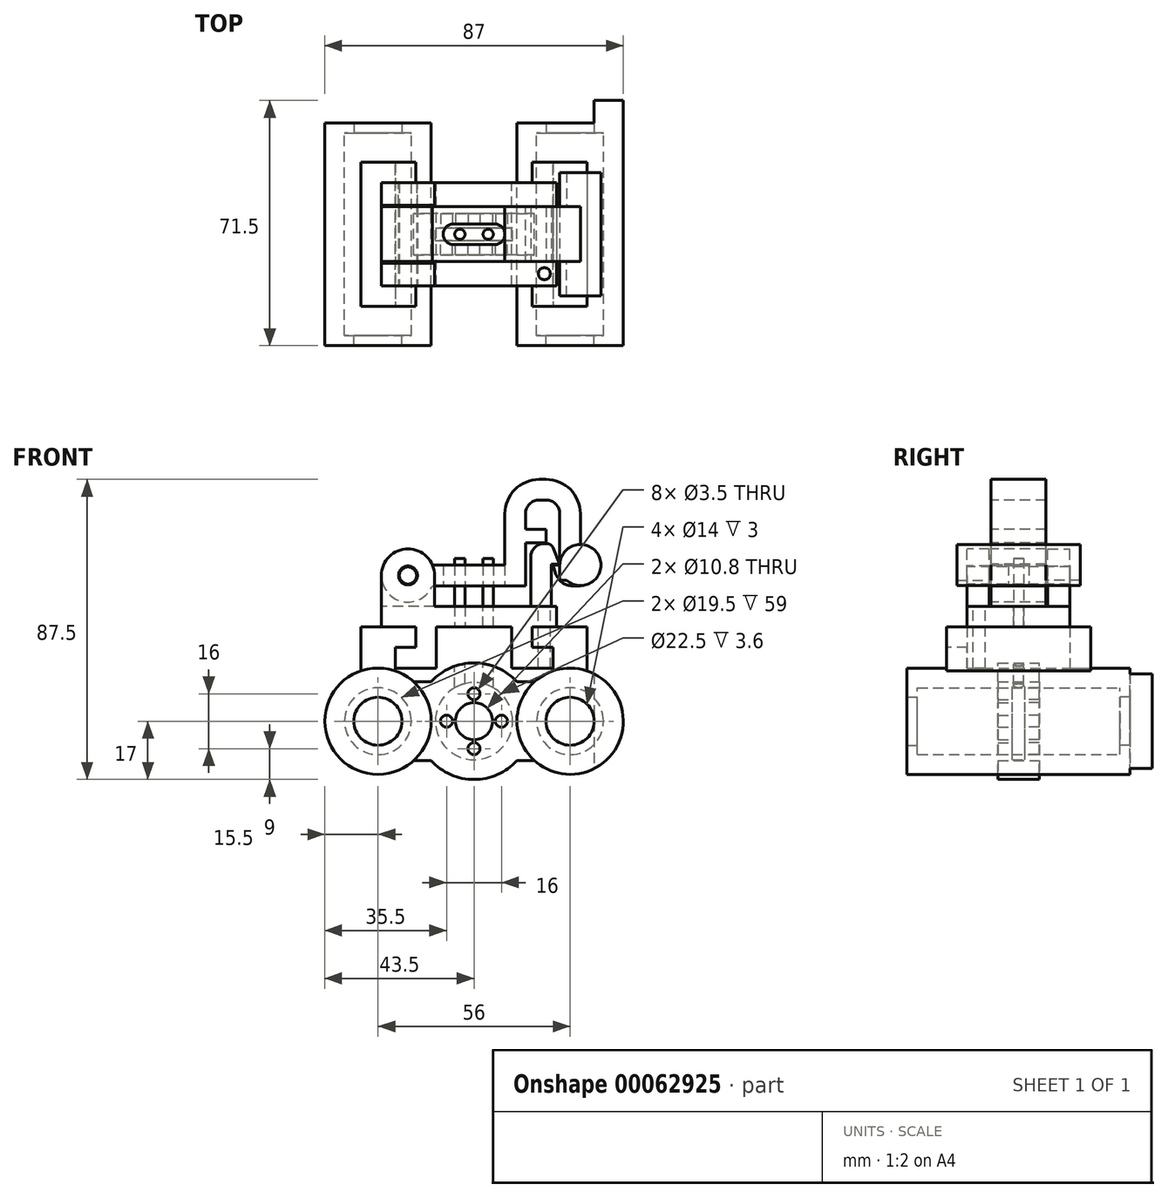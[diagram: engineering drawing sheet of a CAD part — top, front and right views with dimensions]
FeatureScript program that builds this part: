
annotation { "Feature Type Name" : "Feature", "Feature Type Description" : "" }
export const myFeature = defineFeature(function(context is Context, id is Id, definition is map)
    precondition{}
    {
        {
            var Q0;
            Q0=qCreatedBy(makeId("Front.planeOp"),FACE);
            var sketch = newSketch(context, id + "F0", { "sketchPlane" : qUnion([Q0])});
            skCircle(sketch, "E0", {"center": v(0, 0) * mm, "radius": 5.4 * mm});
            skCircle(sketch, "E1", {"center": v(0, 0) * mm, "radius": 11.25 * mm});
            skCircle(sketch, "E2", {"center": v(0, 0) * mm, "radius": 8 * mm, "construction": true});
            skCircle(sketch, "E3", {"center": v(0, 8) * mm, "radius": 1.75 * mm});
            skCircle(sketch, "E4", {"center": v(8, 0) * mm, "radius": 1.75 * mm});
            skCircle(sketch, "E5", {"center": v(0, -8) * mm, "radius": 1.75 * mm});
            skCircle(sketch, "E6", {"center": v(-8, 0) * mm, "radius": 1.75 * mm});
            skArc(sketch, "E7", {"start": v(12.52, 11.5) * mm, "mid": v(0, 17) * mm, "end": v(-12.52, 11.5) * mm});
            skLineSegment(sketch, "E8.bottom", {"start": v(-12.52, 11.5) * mm, "end": v(-17.6, 11.5) * mm});
            skLineSegment(sketch, "E8.top", {"start": v(-12.52, -11.5) * mm, "end": v(-17.6, -11.5) * mm});
            skLineSegment(sketch, "E8.left", {"start": v(-12.52, 11.5) * mm, "end": v(-12.52, -11.5) * mm, "construction": true});
            skLineSegment(sketch, "E9.bottom", {"start": v(12.52, 11.5) * mm, "end": v(17.6, 11.5) * mm});
            skLineSegment(sketch, "E9.top", {"start": v(12.52, -11.5) * mm, "end": v(17.6, -11.5) * mm});
            skLineSegment(sketch, "E9.left", {"start": v(12.52, 11.5) * mm, "end": v(12.52, -11.5) * mm, "construction": true});
            skArc(sketch, "E10", {"start": v(-17.6, 11.5) * mm, "mid": v(-43.5, 0) * mm, "end": v(-17.6, -11.5) * mm});
            skArc(sketch, "E11", {"start": v(17.6, -11.5) * mm, "mid": v(43.5, 0) * mm, "end": v(17.6, 11.5) * mm});
            skCircle(sketch, "E12", {"center": v(-28, 0) * mm, "radius": 9.75 * mm});
            skCircle(sketch, "E13", {"center": v(28, 0) * mm, "radius": 9.75 * mm});
            skLineSegment(sketch, "E14", {"start": v(-28, 0) * mm, "end": v(28, 0) * mm, "construction": true});
            skPoint(sketch, "E15", {"position": v(12.52, 0) * mm});
            skPoint(sketch, "E16", {"position": v(-12.52, 0) * mm});
            skArc(sketch, "E17.trimOffspring", {"start": v(-12.52, -11.5) * mm, "mid": v(0, -17) * mm, "end": v(12.52, -11.5) * mm});
            skSolve(sketch);
        }
        {
            var Q0;
            Q0=makeQuery(id+"F0.imprint","IMPRINT",FACE,{"disambiguationData":[TD([[makeQuery(id+"F0.imprint","IMPRINT",EDGE,{"derivedFrom":sQuery(id+"F0.wireOp",EDGE,"E1")}),-1.0]])]});
            var Q1;
            Q1=makeQuery(id+"F0.imprint","IMPRINT",FACE,{"disambiguationData":[TD([[makeQuery(id+"F0.imprint","IMPRINT",EDGE,{"derivedFrom":sQuery(id+"F0.wireOp",EDGE,"E0")}),-1.0]])]});
            extrude(context, id + "F1", {"entities" : qUnion([Q0, Q1]), "depth" : 6 * mm});
        }
        {
            var Q0;
            Q0=makeQuery(id+"F0.imprint","IMPRINT",FACE,{"disambiguationData":[TD([[makeQuery(id+"F0.imprint","IMPRINT",EDGE,{"derivedFrom":sQuery(id+"F0.wireOp",EDGE,"E0")}),-1.0]])]});
            extrude(context, id + "F2", {"entities" : qUnion([Q0]), "operationType" : NewBodyOperationType.REMOVE, "depth" : 1.8 * mm});
        }
        {
            var Q0;
            Q0=makeQuery(id+"F1.opExtrude","CAP_FACE",FACE,{"disambiguationData":[OSD([sQuery(id+"F0.wireOp",EDGE,"E0"),sQuery(id+"F0.wireOp",EDGE,"E3"),sQuery(id+"F0.wireOp",EDGE,"E4"),sQuery(id+"F0.wireOp",EDGE,"E5"),sQuery(id+"F0.wireOp",EDGE,"E6"),sQuery(id+"F0.wireOp",EDGE,"E7"),sQuery(id+"F0.wireOp",EDGE,"E8.bottom"),sQuery(id+"F0.wireOp",EDGE,"E8.top"),sQuery(id+"F0.wireOp",EDGE,"E9.bottom"),sQuery(id+"F0.wireOp",EDGE,"E9.top"),sQuery(id+"F0.wireOp",EDGE,"E10"),sQuery(id+"F0.wireOp",EDGE,"E11"),sQuery(id+"F0.wireOp",EDGE,"E12"),sQuery(id+"F0.wireOp",EDGE,"E13"),sQuery(id+"F0.wireOp",EDGE,"E17.trimOffspring")])],"isStart":false});
            var sketch = newSketch(context, id + "F3", { "sketchPlane" : qUnion([Q0])});
            skCircle(sketch, "E18", {"center": v(-28, 0) * mm, "radius": 15.5 * mm});
            skCircle(sketch, "E19", {"center": v(-28, 0) * mm, "radius": 9.75 * mm});
            skCircle(sketch, "E20", {"center": v(28, 0) * mm, "radius": 9.75 * mm});
            skCircle(sketch, "E21", {"center": v(28, 0) * mm, "radius": 15.5 * mm});
            skSolve(sketch);
        }
        {
            var Q0;
            Q0 = qSketchRegion(id + "F3", true);
            extrude(context, id + "F4", {"entities" : qUnion([Q0]), "operationType" : NewBodyOperationType.ADD, "depth" : 23.5 * mm});
        }
        {
            var Q0;
            Q0=makeQuery(id+"F4.opExtrude","CAP_FACE",FACE,{"disambiguationData":[OSD([sQuery(id+"F3.wireOp",EDGE,"E18"),sQuery(id+"F3.wireOp",EDGE,"E19")])],"isStart":false});
            var sketch = newSketch(context, id + "F5", { "sketchPlane" : qUnion([Q0])});
            skCircle(sketch, "E22", {"center": v(-28, 0) * mm, "radius": 15.5 * mm});
            skCircle(sketch, "E23", {"center": v(-28, 0) * mm, "radius": 7 * mm});
            skSolve(sketch);
        }
        {
            var Q0;
            Q0 = qSketchRegion(id + "F5", true);
            extrude(context, id + "F6", {"entities" : qUnion([Q0]), "operationType" : NewBodyOperationType.ADD, "depth" : 3 * mm});
        }
        {
            var Q0;
            Q0=makeQuery(id+"F4.opExtrude","CAP_FACE",FACE,{"disambiguationData":[OSD([sQuery(id+"F3.wireOp",EDGE,"E20"),sQuery(id+"F3.wireOp",EDGE,"E21")])],"isStart":false});
            var sketch = newSketch(context, id + "F7", { "sketchPlane" : qUnion([Q0])});
            skCircle(sketch, "E24", {"center": v(28, 0) * mm, "radius": 15.5 * mm});
            skCircle(sketch, "E25", {"center": v(28, 0) * mm, "radius": 7 * mm});
            skSolve(sketch);
        }
        {
            var Q0;
            Q0 = qSketchRegion(id + "F7", true);
            extrude(context, id + "F8", {"entities" : qUnion([Q0]), "operationType" : NewBodyOperationType.ADD, "depth" : 3 * mm});
        }
        {
            var Q0;
            {var subQ0=sQuery(id+"F5.wireOp",EDGE,"E22");Q0=makeQuery(id+"F11.boolean.opBoolean","MERGE",FACE,{"derivedFrom":[makeQuery(id+"F6.opExtrude","CAP_FACE",FACE,{"disambiguationData":[OSD([subQ0,sQuery(id+"F5.wireOp",EDGE,"E23")])],"isStart":false}),makeQuery(id+"F11.opExtrude","CAP_FACE",FACE,{"disambiguationData":[OSD([subQ0,sQuery(id+"F10.wireOp",EDGE,"E26.top"),sQuery(id+"F10.wireOp",EDGE,"E26.left"),sQuery(id+"F10.wireOp",EDGE,"E26.right"),sQuery(id+"F10.wireOp",EDGE,"E27.bottom"),sQuery(id+"F10.wireOp",EDGE,"E27.top"),sQuery(id+"F10.wireOp",EDGE,"E27.right")])],"isStart":true})]});}
            cPlane(context, id + "F9", {"entities" : qUnion([Q0]), "cplaneType" : CPlaneType.OFFSET, "offset" : 11.5 * mm, "oppositeDirection" : true, "width" : 150 * mm, "height" : 150 * mm});
        }
        {
            var Q0;
            Q0=qCreatedBy(id+"F9.planeOp",FACE);
            var sketch = newSketch(context, id + "F10", { "sketchPlane" : qUnion([Q0])});
            skLineSegment(sketch, "E26.top", {"start": v(-33, 27.5) * mm, "end": v(-23, 27.5) * mm});
            skLineSegment(sketch, "E26.left", {"start": v(-33, 14.67) * mm, "end": v(-33, 27.5) * mm});
            skLineSegment(sketch, "E26.right", {"start": v(-23, 14.67) * mm, "end": v(-23, 21.5) * mm});
            skLineSegment(sketch, "E27.bottom", {"start": v(-23, 27.5) * mm, "end": v(-17, 27.5) * mm});
            skLineSegment(sketch, "E27.top", {"start": v(-23, 21.5) * mm, "end": v(-17, 21.5) * mm});
            skLineSegment(sketch, "E27.right", {"start": v(-17, 27.5) * mm, "end": v(-17, 21.5) * mm});
            skLineSegment(sketch, "E28", {"start": v(-28, 0) * mm, "end": v(-28, 27.5) * mm, "construction": true});
            skLineSegment(sketch, "E29", {"start": v(0, 0) * mm, "end": v(0, 38.75) * mm, "construction": true});
            skLineSegment(sketch, "E30.MirrorCS", {"start": v(17, 27.5) * mm, "end": v(17, 21.5) * mm});
            skLineSegment(sketch, "E31.MirrorCS", {"start": v(23, 21.5) * mm, "end": v(17, 21.5) * mm});
            skLineSegment(sketch, "E32.MirrorCS", {"start": v(23, 27.5) * mm, "end": v(17, 27.5) * mm});
            skLineSegment(sketch, "E33.MirrorCS", {"start": v(23, 14.67) * mm, "end": v(23, 21.5) * mm});
            skLineSegment(sketch, "E34.MirrorCS", {"start": v(33, 14.67) * mm, "end": v(33, 27.5) * mm});
            skLineSegment(sketch, "E35.MirrorCS", {"start": v(33, 27.5) * mm, "end": v(23, 27.5) * mm});
            skArc(sketch, "E36", {"start": v(33, 14.67) * mm, "mid": v(28, 15.5) * mm, "end": v(23, 14.67) * mm});
            skArc(sketch, "E37", {"start": v(-23, 14.67) * mm, "mid": v(-28, 15.5) * mm, "end": v(-33, 14.67) * mm});
            skSolve(sketch);
        }
        {
            var Q0;
            Q0 = qSketchRegion(id + "F10", true);
            var Q1;
            Q1=makeQuery(id+"F10.imprint","IMPRINT",FACE,{"disambiguationData":[TD([[makeQuery(id+"F10.imprint","IMPRINT",EDGE,{"derivedFrom":sQuery(id+"F10.wireOp",EDGE,"E26.top")}),-1.0]])]});
            var Q2;
            Q2=makeQuery(id+"F1.opExtrude","CAP_FACE",FACE,{"disambiguationData":[OSD([sQuery(id+"F0.wireOp",EDGE,"E0"),sQuery(id+"F0.wireOp",EDGE,"E3"),sQuery(id+"F0.wireOp",EDGE,"E4"),sQuery(id+"F0.wireOp",EDGE,"E5"),sQuery(id+"F0.wireOp",EDGE,"E6"),sQuery(id+"F0.wireOp",EDGE,"E7"),sQuery(id+"F0.wireOp",EDGE,"E8.bottom"),sQuery(id+"F0.wireOp",EDGE,"E8.top"),sQuery(id+"F0.wireOp",EDGE,"E9.bottom"),sQuery(id+"F0.wireOp",EDGE,"E9.top"),sQuery(id+"F0.wireOp",EDGE,"E10"),sQuery(id+"F0.wireOp",EDGE,"E11"),sQuery(id+"F0.wireOp",EDGE,"E12"),sQuery(id+"F0.wireOp",EDGE,"E13"),sQuery(id+"F0.wireOp",EDGE,"E17.trimOffspring")])],"isStart":true});
            extrude(context, id + "F11", {"entities" : qUnion([Q0, Q1]), "operationType" : NewBodyOperationType.ADD, "endBound" : BoundingType.UP_TO_SURFACE, "oppositeDirection" : true, "endBoundEntityFace" : qUnion([Q2]), "depth" : 25 * mm});
        }
        {
            var Q0;
            Q0=makeQuery(id+"F1.opExtrude","SWEPT_BODY",BODY,{"disambiguationData":[OSD([sQuery(id+"F0.wireOp",EDGE,"E0"),sQuery(id+"F0.wireOp",EDGE,"E3"),sQuery(id+"F0.wireOp",EDGE,"E4"),sQuery(id+"F0.wireOp",EDGE,"E5"),sQuery(id+"F0.wireOp",EDGE,"E6"),sQuery(id+"F0.wireOp",EDGE,"E7"),sQuery(id+"F0.wireOp",EDGE,"E8.bottom"),sQuery(id+"F0.wireOp",EDGE,"E8.top"),sQuery(id+"F0.wireOp",EDGE,"E9.bottom"),sQuery(id+"F0.wireOp",EDGE,"E9.top"),sQuery(id+"F0.wireOp",EDGE,"E10"),sQuery(id+"F0.wireOp",EDGE,"E11"),sQuery(id+"F0.wireOp",EDGE,"E12"),sQuery(id+"F0.wireOp",EDGE,"E13"),sQuery(id+"F0.wireOp",EDGE,"E17.trimOffspring")])]});
            var Q1;
            Q1=qCreatedBy(makeId("Front.planeOp"),FACE);
            mirror(context, id + "F12", {"entities" : qUnion([Q0]), "mirrorPlane" : qUnion([Q1])});
        }
        {
            var Q0;
            Q0=makeQuery(id+"F12.opPattern","COPY",FACE,{"derivedFrom":makeQuery(id+"F11.opExtrude","SWEPT_FACE",FACE,{"disambiguationData":[OSD([sQuery(id+"F10.wireOp",EDGE,"E32.MirrorCS"),sQuery(id+"F10.wireOp",EDGE,"E35.MirrorCS")])]}),"instanceName":"1"});
            var sketch = newSketch(context, id + "F13", { "sketchPlane" : qUnion([Q0])});
            skLineSegment(sketch, "E38.bottom", {"start": v(24, 15) * mm, "end": v(-27, 15) * mm});
            skLineSegment(sketch, "E38.top", {"start": v(24, -15) * mm, "end": v(-27, -15) * mm});
            skLineSegment(sketch, "E38.left", {"start": v(24, 15) * mm, "end": v(24, -15) * mm});
            skLineSegment(sketch, "E38.right", {"start": v(-27, 15) * mm, "end": v(-27, -15) * mm});
            skPoint(sketch, "E39", {"position": v(24, 0) * mm});
            skSolve(sketch);
        }
        {
            var Q0;
            Q0 = qSketchRegion(id + "F13", true);
            extrude(context, id + "F14", {"entities" : qUnion([Q0]), "depth" : 6 * mm});
        }
        {
            var Q0;
            Q0=makeQuery(id+"F14.opExtrude","CAP_FACE",FACE,{"disambiguationData":[OSD([sQuery(id+"F13.wireOp",EDGE,"E38.bottom"),sQuery(id+"F13.wireOp",EDGE,"E38.top"),sQuery(id+"F13.wireOp",EDGE,"E38.left"),sQuery(id+"F13.wireOp",EDGE,"E38.right")])],"isStart":false});
            var sketch = newSketch(context, id + "F15", { "sketchPlane" : qUnion([Q0])});
            skCircle(sketch, "E40", {"center": v(-4.12, 0) * mm, "radius": 1.5 * mm});
            skCircle(sketch, "E41", {"center": v(4.12, 0) * mm, "radius": 1.5 * mm});
            skLineSegment(sketch, "E42", {"start": v(-4.12, 0) * mm, "end": v(4.12, 0) * mm, "construction": true});
            skSolve(sketch);
        }
        {
            var Q0;
            Q0 = qSketchRegion(id + "F15", true);
            extrude(context, id + "F16", {"entities" : qUnion([Q0]), "operationType" : NewBodyOperationType.REMOVE, "oppositeDirection" : true, "depth" : 25 * mm});
        }
        {
            var Q0;
            Q0=makeQuery(id+"F14.opExtrude","CAP_FACE",FACE,{"disambiguationData":[OSD([sQuery(id+"F13.wireOp",EDGE,"E38.bottom"),sQuery(id+"F13.wireOp",EDGE,"E38.top"),sQuery(id+"F13.wireOp",EDGE,"E38.left"),sQuery(id+"F13.wireOp",EDGE,"E38.right")])],"isStart":true});
            var sketch = newSketch(context, id + "F17", { "sketchPlane" : qUnion([Q0])});
            skCircle(sketch, "E43", {"center": v(-4.12, 0) * mm, "radius": 1.5 * mm});
            skCircle(sketch, "E44", {"center": v(4.12, 0) * mm, "radius": 1.5 * mm});
            skSolve(sketch);
        }
        {
            var Q0;
            Q0 = qSketchRegion(id + "F17", true);
            extrude(context, id + "F18", {"entities" : qUnion([Q0]), "oppositeDirection" : true, "depth" : 20 * mm});
        }
        {
            var Q0;
            Q0=makeQuery(id+"F14.opExtrude","CAP_FACE",FACE,{"disambiguationData":[OSD([sQuery(id+"F13.wireOp",EDGE,"E38.bottom"),sQuery(id+"F13.wireOp",EDGE,"E38.top"),sQuery(id+"F13.wireOp",EDGE,"E38.left"),sQuery(id+"F13.wireOp",EDGE,"E38.right")])],"isStart":false});
            cPlane(context, id + "F19", {"entities" : qUnion([Q0]), "cplaneType" : CPlaneType.OFFSET, "offset" : 6 * mm, "width" : 150 * mm, "height" : 150 * mm});
        }
        {
            var Q0;
            Q0=qCreatedBy(id+"F19.planeOp",FACE);
            var sketch = newSketch(context, id + "F20", { "sketchPlane" : qUnion([Q0])});
            skLineSegment(sketch, "E45.bottom", {"start": v(-19.25, -8) * mm, "end": v(15, -8) * mm});
            skLineSegment(sketch, "E45.top", {"start": v(-19.25, 8) * mm, "end": v(15, 8) * mm});
            skLineSegment(sketch, "E45.left", {"start": v(-19.25, -8) * mm, "end": v(-19.25, 8) * mm});
            skLineSegment(sketch, "E45.right", {"start": v(15, -8) * mm, "end": v(15, 8) * mm});
            skLineSegment(sketch, "E46.bottom", {"start": v(-6, -3) * mm, "end": v(6, -3) * mm});
            skLineSegment(sketch, "E46.top", {"start": v(-6, 3) * mm, "end": v(6, 3) * mm});
            skArc(sketch, "E47", {"start": v(-6, -3) * mm, "mid": v(-9, 0) * mm, "end": v(-6, 3) * mm});
            skArc(sketch, "E48", {"start": v(6, -3) * mm, "mid": v(9, 0) * mm, "end": v(6, 3) * mm});
            skLineSegment(sketch, "E49", {"start": v(-19.25, 0) * mm, "end": v(15, 0) * mm, "construction": true});
            skSolve(sketch);
        }
        {
            var Q0;
            Q0 = qSketchRegion(id + "F20", true);
            extrude(context, id + "F21", {"entities" : qUnion([Q0]), "depth" : 6 * mm});
        }
        {
            var Q0;
            Q0=makeQuery(id+"F21.opExtrude","SWEPT_FACE",FACE,{"disambiguationData":[OSD([sQuery(id+"F20.wireOp",EDGE,"E45.bottom")])]});
            var sketch = newSketch(context, id + "F22", { "sketchPlane" : qUnion([Q0])});
            skCircle(sketch, "E50", {"center": v(-19.25, 42.5) * mm, "radius": 2.75 * mm});
            skCircle(sketch, "E51", {"center": v(-19.25, 42.5) * mm, "radius": 7.75 * mm});
            skSolve(sketch);
        }
        {
            var Q0;
            {var subQ0=sQuery(id+"F20.wireOp",EDGE,"E45.bottom");var subQ6=sQuery(id+"F22.wireOp",EDGE,"E51");var subQ7=makeQuery(id+"F21.opExtrude","CAP_EDGE",EDGE,{"disambiguationData":[OSD([subQ0])],"isStart":true});var subQ8=makeQuery(id+"F22.imprint","INTERSECT",VERTEX,{"derivedFrom":[subQ7,subQ6]});Q0=makeQuery(id+"F22.imprint","IMPRINT",FACE,{"disambiguationData":[TD([[makeQuery(id+"F22.imprint","IMPRINT",EDGE,{"disambiguationData":[TD([[subQ8,1.0]])],"derivedFrom":subQ6}),1.0]])]});}
            var Q1;
            Q1=makeQuery(id+"F21.opExtrude","SWEPT_FACE",FACE,{"disambiguationData":[OSD([sQuery(id+"F20.wireOp",EDGE,"E45.top")])]});
            extrude(context, id + "F23", {"entities" : qUnion([Q0]), "operationType" : NewBodyOperationType.ADD, "endBound" : BoundingType.UP_TO_SURFACE, "oppositeDirection" : true, "endBoundEntityFace" : qUnion([Q1]), "depth" : 25 * mm});
        }
        {
            var Q0;
            {var subQ0=sQuery(id+"F22.wireOp",EDGE,"E50");var subQ1=makeQuery(id+"F21.opExtrude","SWEPT_EDGE",EDGE,{"disambiguationData":[OSD([sQuery(id+"F20.wireOp",EDGE,"E45.bottom"),sQuery(id+"F20.wireOp",EDGE,"E45.left")])]});var subQ2=makeQuery(id+"F22.imprint","INTERSECT",VERTEX,{"disambiguationData":[OD(0.0)],"derivedFrom":[subQ1,subQ0]});Q0=makeQuery(id+"F22.imprint","IMPRINT",FACE,{"disambiguationData":[TD([[makeQuery(id+"F22.imprint","IMPRINT",EDGE,{"disambiguationData":[TD([[subQ2,-1.0]])],"derivedFrom":subQ0}),1.0]])]});}
            var Q1;
            Q1=makeQuery(id+"F23.boolean.opBoolean","MERGE",FACE,{"derivedFrom":[makeQuery(id+"F21.opExtrude","SWEPT_FACE",FACE,{"disambiguationData":[OSD([sQuery(id+"F20.wireOp",EDGE,"E45.top")])]}),makeQuery(id+"F23.opExtrude","CAP_FACE",FACE,{"disambiguationData":[OSD([sQuery(id+"F20.wireOp",EDGE,"E45.bottom"),sQuery(id+"F20.wireOp",EDGE,"E45.left"),sQuery(id+"F22.wireOp",EDGE,"E50"),sQuery(id+"F22.wireOp",EDGE,"E51")])],"isStart":false})]});
            extrude(context, id + "F24", {"entities" : qUnion([Q0]), "operationType" : NewBodyOperationType.REMOVE, "endBound" : BoundingType.UP_TO_SURFACE, "oppositeDirection" : true, "endBoundEntityFace" : qUnion([Q1]), "depth" : 25 * mm});
        }
        {
            var Q0;
            Q0=makeQuery(id+"F14.opExtrude","SWEPT_FACE",FACE,{"disambiguationData":[OSD([sQuery(id+"F13.wireOp",EDGE,"E38.top")])]});
            var sketch = newSketch(context, id + "F25", { "sketchPlane" : qUnion([Q0])});
            skLineSegment(sketch, "E52.bottom", {"start": v(-27, 33.5) * mm, "end": v(-11.5, 33.5) * mm});
            skLineSegment(sketch, "E52.left", {"start": v(-27, 33.5) * mm, "end": v(-27, 42.5) * mm});
            skLineSegment(sketch, "E52.right", {"start": v(-11.5, 33.5) * mm, "end": v(-11.5, 42.5) * mm});
            skArc(sketch, "E53", {"start": v(-11.5, 42.5) * mm, "mid": v(-19.25, 50.25) * mm, "end": v(-27, 42.5) * mm});
            skCircle(sketch, "E54", {"center": v(-19.25, 42.5) * mm, "radius": 2.75 * mm});
            skSolve(sketch);
        }
        {
            var Q0;
            Q0 = qSketchRegion(id + "F25", true);
            var Q1;
            {var subQ2=sQuery(id+"F25.wireOp",EDGE,"E52.bottom");Q1=makeQuery(id+"F25.imprint","IMPRINT",FACE,{"disambiguationData":[TD([[makeQuery(id+"F25.imprint","IMPRINT",EDGE,{"derivedFrom":subQ2}),1.0]])]});}
            extrude(context, id + "F26", {"entities" : qUnion([Q0, Q1]), "operationType" : NewBodyOperationType.ADD, "oppositeDirection" : true, "depth" : 6.5 * mm});
        }
        {
            var Q0;
            Q0=makeQuery(id+"F14.opExtrude","SWEPT_FACE",FACE,{"disambiguationData":[OSD([sQuery(id+"F13.wireOp",EDGE,"E38.bottom")])]});
            var sketch = newSketch(context, id + "F27", { "sketchPlane" : qUnion([Q0])});
            skLineSegment(sketch, "E55.bottom", {"start": v(27, 33.5) * mm, "end": v(11.5, 33.5) * mm});
            skLineSegment(sketch, "E55.left", {"start": v(27, 33.5) * mm, "end": v(27, 42.5) * mm});
            skLineSegment(sketch, "E55.right", {"start": v(11.5, 33.5) * mm, "end": v(11.5, 42.5) * mm});
            skArc(sketch, "E56", {"start": v(27, 42.5) * mm, "mid": v(19.25, 50.25) * mm, "end": v(11.5, 42.5) * mm});
            skCircle(sketch, "E57", {"center": v(19.25, 42.5) * mm, "radius": 2.75 * mm});
            skSolve(sketch);
        }
        {
            var Q0;
            Q0 = qSketchRegion(id + "F27", true);
            var Q1;
            {var subQ1=sQuery(id+"F27.wireOp",EDGE,"E55.bottom");Q1=makeQuery(id+"F27.imprint","IMPRINT",FACE,{"disambiguationData":[TD([[makeQuery(id+"F27.imprint","IMPRINT",EDGE,{"derivedFrom":subQ1}),-1.0]])]});}
            extrude(context, id + "F28", {"entities" : qUnion([Q0, Q1]), "operationType" : NewBodyOperationType.ADD, "oppositeDirection" : true, "depth" : 6.5 * mm});
        }
        {
            var Q0;
            {var subQ0=sQuery(id+"F13.wireOp",EDGE,"E38.top");Q0=makeQuery(id+"F26.boolean.opBoolean","MERGE",FACE,{"derivedFrom":[makeQuery(id+"F14.opExtrude","SWEPT_FACE",FACE,{"disambiguationData":[OSD([subQ0])]}),makeQuery(id+"F26.opExtrude","CAP_FACE",FACE,{"disambiguationData":[OSD([subQ0,sQuery(id+"F13.wireOp",EDGE,"E38.left"),sQuery(id+"F13.wireOp",EDGE,"E38.right"),sQuery(id+"F25.wireOp",EDGE,"E52.left"),sQuery(id+"F25.wireOp",EDGE,"E52.right"),sQuery(id+"F25.wireOp",EDGE,"E53"),sQuery(id+"F25.wireOp",EDGE,"E54")])],"isStart":true})]});}
            var sketch = newSketch(context, id + "F29", { "sketchPlane" : qUnion([Q0])});
            skCircle(sketch, "E58", {"center": v(-19.25, 42.5) * mm, "radius": 2.5 * mm});
            skSolve(sketch);
        }
        {
            var Q0;
            Q0 = qSketchRegion(id + "F29", true);
            var Q1;
            {var subQ0=sQuery(id+"F13.wireOp",EDGE,"E38.bottom");Q1=makeQuery(id+"F28.boolean.opBoolean","MERGE",FACE,{"derivedFrom":[makeQuery(id+"F14.opExtrude","SWEPT_FACE",FACE,{"disambiguationData":[OSD([subQ0])]}),makeQuery(id+"F28.opExtrude","CAP_FACE",FACE,{"disambiguationData":[OSD([sQuery(id+"F10.wireOp",EDGE,"E34.MirrorCS"),sQuery(id+"F10.wireOp",EDGE,"E35.MirrorCS"),subQ0,sQuery(id+"F13.wireOp",EDGE,"E38.left"),sQuery(id+"F13.wireOp",EDGE,"E38.right"),sQuery(id+"F27.wireOp",EDGE,"E55.left"),sQuery(id+"F27.wireOp",EDGE,"E55.right"),sQuery(id+"F27.wireOp",EDGE,"E56"),sQuery(id+"F27.wireOp",EDGE,"E57")])],"isStart":true})]});}
            extrude(context, id + "F30", {"entities" : qUnion([Q0]), "endBound" : BoundingType.UP_TO_SURFACE, "oppositeDirection" : true, "endBoundEntityFace" : qUnion([Q1]), "depth" : 25 * mm});
        }
        {
            var Q0;
            {var subQ0=sQuery(id+"F20.wireOp",EDGE,"E45.bottom");Q0=makeQuery(id+"F23.boolean.opBoolean","MERGE",FACE,{"derivedFrom":[makeQuery(id+"F21.opExtrude","SWEPT_FACE",FACE,{"disambiguationData":[OSD([subQ0])]}),makeQuery(id+"F23.opExtrude","CAP_FACE",FACE,{"disambiguationData":[OSD([subQ0,sQuery(id+"F20.wireOp",EDGE,"E45.left"),sQuery(id+"F22.wireOp",EDGE,"E50"),sQuery(id+"F22.wireOp",EDGE,"E51")])],"isStart":true})]});}
            var sketch = newSketch(context, id + "F31", { "sketchPlane" : qUnion([Q0])});
            skLineSegment(sketch, "E59", {"start": v(9, 45.5) * mm, "end": v(9, 60.5) * mm});
            skLineSegment(sketch, "E60", {"start": v(19, 70.5) * mm, "end": v(21, 70.5) * mm});
            skLineSegment(sketch, "E61", {"start": v(31, 60.5) * mm, "end": v(31, 39.5) * mm});
            skLineSegment(sketch, "E62", {"start": v(31, 39.5) * mm, "end": v(28.6, 39.5) * mm});
            skLineSegment(sketch, "E63", {"start": v(23.86, 42.92) * mm, "end": v(23, 45.5) * mm});
            skLineSegment(sketch, "E64", {"start": v(23, 45.5) * mm, "end": v(25, 45.5) * mm});
            skLineSegment(sketch, "E65", {"start": v(25, 45.5) * mm, "end": v(25, 60.5) * mm});
            skLineSegment(sketch, "E66", {"start": v(21, 64.5) * mm, "end": v(19, 64.5) * mm});
            skLineSegment(sketch, "E67", {"start": v(15, 60.5) * mm, "end": v(15, 45.5) * mm});
            skPoint(sketch, "E68.visualSharp", {"position": v(9, 70.5) * mm});
            skArc(sketch, "E68.filletArc", {"start": v(19, 70.5) * mm, "mid": v(11.93, 67.57) * mm, "end": v(9, 60.5) * mm});
            skPoint(sketch, "E69.visualSharp", {"position": v(15, 64.5) * mm});
            skArc(sketch, "E69.filletArc", {"start": v(19, 64.5) * mm, "mid": v(16.17, 63.33) * mm, "end": v(15, 60.5) * mm});
            skPoint(sketch, "E70.visualSharp", {"position": v(31, 70.5) * mm});
            skArc(sketch, "E70.filletArc", {"start": v(31, 60.5) * mm, "mid": v(28.07, 67.57) * mm, "end": v(21, 70.5) * mm});
            skPoint(sketch, "E71.visualSharp", {"position": v(25, 64.5) * mm});
            skArc(sketch, "E71.filletArc", {"start": v(25, 60.5) * mm, "mid": v(23.83, 63.33) * mm, "end": v(21, 64.5) * mm});
            skLineSegment(sketch, "E72", {"start": v(9, 45.5) * mm, "end": v(15, 45.5) * mm});
            skLineSegment(sketch, "E73.bottom", {"start": v(15, 56) * mm, "end": v(21, 56) * mm});
            skLineSegment(sketch, "E73.top", {"start": v(15, 52) * mm, "end": v(21, 52) * mm});
            skLineSegment(sketch, "E73.left", {"start": v(15, 56) * mm, "end": v(15, 52) * mm});
            skLineSegment(sketch, "E73.right", {"start": v(21, 56) * mm, "end": v(21, 52) * mm});
            skPoint(sketch, "E74.visualSharp", {"position": v(25, 39.5) * mm});
            skArc(sketch, "E74.filletArc", {"start": v(23.86, 42.92) * mm, "mid": v(25.68, 40.44) * mm, "end": v(28.6, 39.5) * mm});
            skSolve(sketch);
        }
        {
            var Q0;
            Q0 = qSketchRegion(id + "F31", true);
            var Q1;
            Q1=makeQuery(id+"F23.boolean.opBoolean","MERGE",FACE,{"derivedFrom":[makeQuery(id+"F21.opExtrude","SWEPT_FACE",FACE,{"disambiguationData":[OSD([sQuery(id+"F20.wireOp",EDGE,"E45.top")])]}),makeQuery(id+"F23.opExtrude","CAP_FACE",FACE,{"disambiguationData":[OSD([sQuery(id+"F20.wireOp",EDGE,"E45.bottom"),sQuery(id+"F20.wireOp",EDGE,"E45.left"),sQuery(id+"F22.wireOp",EDGE,"E50"),sQuery(id+"F22.wireOp",EDGE,"E51")])],"isStart":false})]});
            extrude(context, id + "F32", {"entities" : qUnion([Q0]), "operationType" : NewBodyOperationType.ADD, "endBound" : BoundingType.UP_TO_SURFACE, "oppositeDirection" : true, "endBoundEntityFace" : qUnion([Q1]), "depth" : 25 * mm});
        }
        {
            var Q0;
            {var subQ0=sQuery(id+"F20.wireOp",EDGE,"E45.bottom");Q0=makeQuery(id+"F32.boolean.opBoolean","MERGE",FACE,{"derivedFrom":[makeQuery(id+"F23.boolean.opBoolean","MERGE",FACE,{"derivedFrom":[makeQuery(id+"F21.opExtrude","SWEPT_FACE",FACE,{"disambiguationData":[OSD([subQ0])]}),makeQuery(id+"F23.opExtrude","CAP_FACE",FACE,{"disambiguationData":[OSD([subQ0,sQuery(id+"F20.wireOp",EDGE,"E45.left"),sQuery(id+"F22.wireOp",EDGE,"E50"),sQuery(id+"F22.wireOp",EDGE,"E51")])],"isStart":true})]}),makeQuery(id+"F32.opExtrude","CAP_FACE",FACE,{"disambiguationData":[OSD([sQuery(id+"F31.wireOp",EDGE,"5079acd1-eaac-4507-bca1-516ebb47fa8f"),sQuery(id+"F31.wireOp",EDGE,"82dcc8e1-da9b-4338-850f-ae2697795ad2"),sQuery(id+"F31.wireOp",EDGE,"v46wGmbz-xF6Q-51pb-38RE-oWoljmZ9v5JP"),sQuery(id+"F31.wireOp",EDGE,"4d731f38-e2de-4b35-94f0-ffd8c3d27091.bottom"),sQuery(id+"F31.wireOp",EDGE,"4d731f38-e2de-4b35-94f0-ffd8c3d27091.left"),sQuery(id+"F31.wireOp",EDGE,"4d731f38-e2de-4b35-94f0-ffd8c3d27091.right"),sQuery(id+"F31.wireOp",EDGE,"0a39d5b3-3a2a-493f-8220-f63ec6ca32e2.bottom"),sQuery(id+"F31.wireOp",EDGE,"0a39d5b3-3a2a-493f-8220-f63ec6ca32e2.top"),sQuery(id+"F31.wireOp",EDGE,"0a39d5b3-3a2a-493f-8220-f63ec6ca32e2.left"),sQuery(id+"F31.wireOp",EDGE,"45f73411-8ce3-4968-b567-3c25bc21c99c.top"),sQuery(id+"F31.wireOp",EDGE,"45f73411-8ce3-4968-b567-3c25bc21c99c.left"),sQuery(id+"F31.wireOp",EDGE,"45f73411-8ce3-4968-b567-3c25bc21c99c.right"),sQuery(id+"F31.wireOp",EDGE,"ByrJsz3G-Q0Oq-3CNk-jIkp-fLPtCC3wEZpb"),sQuery(id+"F31.wireOp",EDGE,"mAN19z1q-9uuv-X1AW-9HnC-pkhjFqnwcaoK")])],"isStart":true})]});}
            var sketch = newSketch(context, id + "F33", { "sketchPlane" : qUnion([Q0])});
            skLineSegment(sketch, "E75.bottom", {"start": v(20.5, 51.8) * mm, "end": v(21.17, 51.8) * mm});
            skLineSegment(sketch, "E75.top", {"start": v(16.5, 33.5) * mm, "end": v(22.5, 33.5) * mm});
            skLineSegment(sketch, "E75.left", {"start": v(16.5, 47.8) * mm, "end": v(16.5, 33.5) * mm});
            skLineSegment(sketch, "E75.right", {"start": v(22.5, 45.8) * mm, "end": v(22.5, 33.5) * mm});
            skLineSegment(sketch, "E76", {"start": v(23.01, 50.57) * mm, "end": v(25, 45.8) * mm});
            skLineSegment(sketch, "E77", {"start": v(22.5, 45.8) * mm, "end": v(25, 45.8) * mm});
            skPoint(sketch, "E78.visualSharp", {"position": v(16.5, 51.8) * mm});
            skArc(sketch, "E78.filletArc", {"start": v(20.5, 51.8) * mm, "mid": v(17.67, 50.63) * mm, "end": v(16.5, 47.8) * mm});
            skPoint(sketch, "E79.visualSharp", {"position": v(22.5, 51.8) * mm});
            skArc(sketch, "E79.filletArc", {"start": v(23.01, 50.57) * mm, "mid": v(22.28, 51.46) * mm, "end": v(21.17, 51.8) * mm});
            skSolve(sketch);
        }
        {
            var Q0;
            Q0 = qSketchRegion(id + "F33", true);
            var Q1;
            Q1=makeQuery(id+"F32.boolean.opBoolean","MERGE",FACE,{"derivedFrom":[makeQuery(id+"F23.boolean.opBoolean","MERGE",FACE,{"derivedFrom":[makeQuery(id+"F21.opExtrude","SWEPT_FACE",FACE,{"disambiguationData":[OSD([sQuery(id+"F20.wireOp",EDGE,"E45.top")])]}),makeQuery(id+"F23.opExtrude","CAP_FACE",FACE,{"disambiguationData":[OSD([sQuery(id+"F20.wireOp",EDGE,"E45.bottom"),sQuery(id+"F20.wireOp",EDGE,"E45.left"),sQuery(id+"F22.wireOp",EDGE,"E50"),sQuery(id+"F22.wireOp",EDGE,"E51")])],"isStart":false})]}),makeQuery(id+"F32.opExtrude","CAP_FACE",FACE,{"disambiguationData":[OSD([sQuery(id+"F31.wireOp",EDGE,"5079acd1-eaac-4507-bca1-516ebb47fa8f"),sQuery(id+"F31.wireOp",EDGE,"82dcc8e1-da9b-4338-850f-ae2697795ad2"),sQuery(id+"F31.wireOp",EDGE,"v46wGmbz-xF6Q-51pb-38RE-oWoljmZ9v5JP"),sQuery(id+"F31.wireOp",EDGE,"4d731f38-e2de-4b35-94f0-ffd8c3d27091.bottom"),sQuery(id+"F31.wireOp",EDGE,"4d731f38-e2de-4b35-94f0-ffd8c3d27091.left"),sQuery(id+"F31.wireOp",EDGE,"4d731f38-e2de-4b35-94f0-ffd8c3d27091.right"),sQuery(id+"F31.wireOp",EDGE,"0a39d5b3-3a2a-493f-8220-f63ec6ca32e2.bottom"),sQuery(id+"F31.wireOp",EDGE,"0a39d5b3-3a2a-493f-8220-f63ec6ca32e2.top"),sQuery(id+"F31.wireOp",EDGE,"0a39d5b3-3a2a-493f-8220-f63ec6ca32e2.left"),sQuery(id+"F31.wireOp",EDGE,"45f73411-8ce3-4968-b567-3c25bc21c99c.top"),sQuery(id+"F31.wireOp",EDGE,"45f73411-8ce3-4968-b567-3c25bc21c99c.left"),sQuery(id+"F31.wireOp",EDGE,"45f73411-8ce3-4968-b567-3c25bc21c99c.right"),sQuery(id+"F31.wireOp",EDGE,"ByrJsz3G-Q0Oq-3CNk-jIkp-fLPtCC3wEZpb"),sQuery(id+"F31.wireOp",EDGE,"mAN19z1q-9uuv-X1AW-9HnC-pkhjFqnwcaoK")])],"isStart":false})]});
            extrude(context, id + "F34", {"entities" : qUnion([Q0]), "operationType" : NewBodyOperationType.ADD, "endBound" : BoundingType.UP_TO_SURFACE, "oppositeDirection" : true, "endBoundEntityFace" : qUnion([Q1]), "depth" : 25 * mm});
        }
        {
            var Q0;
            {var subQ0=sQuery(id+"F13.wireOp",EDGE,"E38.bottom");Q0=makeQuery(id+"F28.boolean.opBoolean","MERGE",FACE,{"derivedFrom":[makeQuery(id+"F14.opExtrude","SWEPT_FACE",FACE,{"disambiguationData":[OSD([subQ0])]}),makeQuery(id+"F28.opExtrude","CAP_FACE",FACE,{"disambiguationData":[OSD([sQuery(id+"F10.wireOp",EDGE,"E34.MirrorCS"),sQuery(id+"F10.wireOp",EDGE,"E35.MirrorCS"),subQ0,sQuery(id+"F13.wireOp",EDGE,"E38.left"),sQuery(id+"F13.wireOp",EDGE,"E38.right"),sQuery(id+"F27.wireOp",EDGE,"E55.left"),sQuery(id+"F27.wireOp",EDGE,"E55.right"),sQuery(id+"F27.wireOp",EDGE,"E56"),sQuery(id+"F27.wireOp",EDGE,"E57")])],"isStart":true})]});}
            var sketch = newSketch(context, id + "F35", { "sketchPlane" : qUnion([Q0])});
            skLineSegment(sketch, "E80.bottom", {"start": v(-11, 27.5) * mm, "end": v(-17, 27.5) * mm});
            skLineSegment(sketch, "E80.top", {"start": v(-11, 15.5) * mm, "end": v(-17, 15.5) * mm});
            skLineSegment(sketch, "E80.left", {"start": v(-11, 27.5) * mm, "end": v(-11, 15.5) * mm});
            skLineSegment(sketch, "E80.right", {"start": v(-17, 27.5) * mm, "end": v(-17, 21.5) * mm});
            skLineSegment(sketch, "E81.bottom", {"start": v(-17, 15.5) * mm, "end": v(-23, 15.5) * mm});
            skLineSegment(sketch, "E81.top", {"start": v(-17, 21.5) * mm, "end": v(-23, 21.5) * mm});
            skLineSegment(sketch, "E81.right", {"start": v(-23, 15.5) * mm, "end": v(-23, 21.5) * mm});
            skLineSegment(sketch, "E82", {"start": v(0, 27.5) * mm, "end": v(0, 19.84) * mm, "construction": true});
            skLineSegment(sketch, "E83.MirrorCS", {"start": v(11, 27.5) * mm, "end": v(11, 15.5) * mm});
            skLineSegment(sketch, "E84.MirrorCS", {"start": v(17, 27.5) * mm, "end": v(17, 21.5) * mm});
            skLineSegment(sketch, "E85.MirrorCS", {"start": v(11, 27.5) * mm, "end": v(17, 27.5) * mm});
            skLineSegment(sketch, "E86.MirrorCS", {"start": v(11, 15.5) * mm, "end": v(17, 15.5) * mm});
            skLineSegment(sketch, "E87.MirrorCS", {"start": v(17, 15.5) * mm, "end": v(23, 15.5) * mm});
            skLineSegment(sketch, "E88.MirrorCS", {"start": v(23, 15.5) * mm, "end": v(23, 21.5) * mm});
            skLineSegment(sketch, "E89.MirrorCS", {"start": v(17, 21.5) * mm, "end": v(23, 21.5) * mm});
            skSolve(sketch);
        }
        {
            var Q0;
            Q0 = qSketchRegion(id + "F35", true);
            var Q1;
            {var subQ0=sQuery(id+"F13.wireOp",EDGE,"E38.top");Q1=makeQuery(id+"F26.boolean.opBoolean","MERGE",FACE,{"derivedFrom":[makeQuery(id+"F14.opExtrude","SWEPT_FACE",FACE,{"disambiguationData":[OSD([subQ0])]}),makeQuery(id+"F26.opExtrude","CAP_FACE",FACE,{"disambiguationData":[OSD([subQ0,sQuery(id+"F13.wireOp",EDGE,"E38.left"),sQuery(id+"F13.wireOp",EDGE,"E38.right"),sQuery(id+"F25.wireOp",EDGE,"E52.bottom"),sQuery(id+"F25.wireOp",EDGE,"E52.left"),sQuery(id+"F25.wireOp",EDGE,"E52.right"),sQuery(id+"F25.wireOp",EDGE,"E53"),sQuery(id+"F25.wireOp",EDGE,"E54")])],"isStart":true})]});}
            extrude(context, id + "F36", {"entities" : qUnion([Q0]), "operationType" : NewBodyOperationType.ADD, "endBound" : BoundingType.UP_TO_SURFACE, "oppositeDirection" : true, "endBoundEntityFace" : qUnion([Q1]), "depth" : 25 * mm});
        }
        {
            var Q0;
            Q0=makeQuery(id+"F11.opExtrude","SWEPT_FACE",FACE,{"disambiguationData":[OSD([sQuery(id+"F10.wireOp",EDGE,"E27.top")])]});
            var sketch = newSketch(context, id + "F37", { "sketchPlane" : qUnion([Q0])});
            skLineSegment(sketch, "E90.rect.bottom", {"start": v(17, -15) * mm, "end": v(23, -15) * mm});
            skLineSegment(sketch, "E90.rect.top", {"start": v(17, -21) * mm, "end": v(23, -21) * mm});
            skLineSegment(sketch, "E90.rect.left", {"start": v(17, -15) * mm, "end": v(17, -21) * mm});
            skLineSegment(sketch, "E90.rect.right", {"start": v(23, -15) * mm, "end": v(23, -21) * mm});
            skPoint(sketch, "E90.rect.middle", {"position": v(20, -18) * mm});
            skLineSegment(sketch, "E91.rect.bottom", {"start": v(-17, -15) * mm, "end": v(-23, -15) * mm});
            skLineSegment(sketch, "E91.rect.top", {"start": v(-17, -21) * mm, "end": v(-23, -21) * mm});
            skLineSegment(sketch, "E91.rect.left", {"start": v(-17, -15) * mm, "end": v(-17, -21) * mm});
            skLineSegment(sketch, "E91.rect.right", {"start": v(-23, -15) * mm, "end": v(-23, -21) * mm});
            skPoint(sketch, "E91.rect.middle", {"position": v(-20, -18) * mm});
            skSolve(sketch);
        }
        {
            var Q0;
            Q0 = qSketchRegion(id + "F37", true);
            extrude(context, id + "F38", {"entities" : qUnion([Q0]), "operationType" : NewBodyOperationType.ADD, "depth" : 6 * mm});
        }
        {
            var Q0;
            Q0=makeQuery(id+"F32.boolean.opBoolean","MERGE",FACE,{"derivedFrom":[makeQuery(id+"F23.boolean.opBoolean","MERGE",FACE,{"derivedFrom":[makeQuery(id+"F21.opExtrude","SWEPT_FACE",FACE,{"disambiguationData":[OSD([sQuery(id+"F20.wireOp",EDGE,"E45.top")])]}),makeQuery(id+"F23.opExtrude","CAP_FACE",FACE,{"disambiguationData":[OSD([sQuery(id+"F20.wireOp",EDGE,"E45.bottom"),sQuery(id+"F20.wireOp",EDGE,"E45.left"),sQuery(id+"F22.wireOp",EDGE,"E50"),sQuery(id+"F22.wireOp",EDGE,"E51")])],"isStart":false})]}),makeQuery(id+"F32.opExtrude","CAP_FACE",FACE,{"disambiguationData":[OSD([sQuery(id+"F31.wireOp",EDGE,"E59"),sQuery(id+"F31.wireOp",EDGE,"E60"),sQuery(id+"F31.wireOp",EDGE,"E61"),sQuery(id+"F31.wireOp",EDGE,"E62"),sQuery(id+"F31.wireOp",EDGE,"E63"),sQuery(id+"F31.wireOp",EDGE,"E64"),sQuery(id+"F31.wireOp",EDGE,"E65"),sQuery(id+"F31.wireOp",EDGE,"E66"),sQuery(id+"F31.wireOp",EDGE,"E67"),sQuery(id+"F31.wireOp",EDGE,"E68.filletArc"),sQuery(id+"F31.wireOp",EDGE,"E69.filletArc"),sQuery(id+"F31.wireOp",EDGE,"E70.filletArc"),sQuery(id+"F31.wireOp",EDGE,"E71.filletArc"),sQuery(id+"F31.wireOp",EDGE,"E72"),sQuery(id+"F31.wireOp",EDGE,"E73.bottom"),sQuery(id+"F31.wireOp",EDGE,"E73.top"),sQuery(id+"F31.wireOp",EDGE,"E73.right"),sQuery(id+"F31.wireOp",EDGE,"E74.filletArc")])],"isStart":false})]});
            var sketch = newSketch(context, id + "F39", { "sketchPlane" : qUnion([Q0])});
            skLineSegment(sketch, "E92.bottom", {"start": v(-31, 41.03) * mm, "end": v(-25, 41.03) * mm});
            skLineSegment(sketch, "E92.top", {"start": v(-31, 51.53) * mm, "end": v(-31, 51.53) * mm});
            skLineSegment(sketch, "E92.left", {"start": v(-31, 41.03) * mm, "end": v(-31, 51.53) * mm});
            skLineSegment(sketch, "E92.right", {"start": v(-25, 41.03) * mm, "end": v(-25, 45.53) * mm});
            skPoint(sketch, "E93.visualSharp", {"position": v(-25, 51.53) * mm});
            skArc(sketch, "E93.filletArc", {"start": v(-25, 45.53) * mm, "mid": v(-26.76, 49.78) * mm, "end": v(-31, 51.53) * mm});
            skCircle(sketch, "E94", {"center": v(-31, 45.53) * mm, "radius": 6 * mm});
            skSolve(sketch);
        }
        {
            var Q0;
            Q0 = qSketchRegion(id + "F39", true);
            extrude(context, id + "F40", {"entities" : qUnion([Q0]), "operationType" : NewBodyOperationType.ADD, "depth" : 10 * mm});
        }
        {
            var Q0;
            Q0 = qSketchRegion(id + "F39", true);
            extrude(context, id + "F41", {"entities" : qUnion([Q0]), "operationType" : NewBodyOperationType.ADD, "oppositeDirection" : true, "depth" : 26 * mm});
        }
        {
            var Q0;
            Q0=makeQuery(id+"F14.opExtrude","CAP_FACE",FACE,{"disambiguationData":[OSD([sQuery(id+"F13.wireOp",EDGE,"E38.bottom"),sQuery(id+"F13.wireOp",EDGE,"E38.top"),sQuery(id+"F13.wireOp",EDGE,"E38.left"),sQuery(id+"F13.wireOp",EDGE,"E38.right")])],"isStart":false});
            var sketch = newSketch(context, id + "F42", { "sketchPlane" : qUnion([Q0])});
            skCircle(sketch, "E95", {"center": v(20.5, -11.5) * mm, "radius": 1.75 * mm});
            skSolve(sketch);
        }
        {
            var Q0;
            Q0 = qSketchRegion(id + "F42", true);
            var Q1;
            Q1=makeQuery(id+"F36.opExtrude","SWEPT_FACE",FACE,{"disambiguationData":[OSD([sQuery(id+"F35.wireOp",EDGE,"E80.top"),sQuery(id+"F35.wireOp",EDGE,"E81.bottom")])]});
            extrude(context, id + "F43", {"entities" : qUnion([Q0]), "operationType" : NewBodyOperationType.REMOVE, "endBound" : BoundingType.UP_TO_SURFACE, "oppositeDirection" : true, "endBoundEntityFace" : qUnion([Q1]), "depth" : 25 * mm});
        }
        {
            var Q0;
            Q0=makeQuery(id+"F12.opPattern","COPY",FACE,{"derivedFrom":makeQuery(id+"F8.opExtrude","CAP_FACE",FACE,{"disambiguationData":[OSD([sQuery(id+"F7.wireOp",EDGE,"E24"),sQuery(id+"F7.wireOp",EDGE,"E25")])],"isStart":false}),"instanceName":"1"});
            var sketch = newSketch(context, id + "F44", { "sketchPlane" : qUnion([Q0])});
            skArc(sketch, "E96", {"start": v(-35, 13.83) * mm, "mid": v(-43.5, 0) * mm, "end": v(-35, -13.83) * mm});
            skLineSegment(sketch, "E97", {"start": v(-35, 13.83) * mm, "end": v(-35, -13.83) * mm});
            skPoint(sketch, "E98", {"position": v(-35, 0) * mm});
            skSolve(sketch);
        }
        {
            var Q0;
            Q0 = qSketchRegion(id + "F44", true);
            extrude(context, id + "F45", {"entities" : qUnion([Q0]), "operationType" : NewBodyOperationType.ADD, "depth" : 6.5 * mm});
        }
    });
